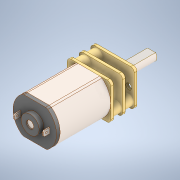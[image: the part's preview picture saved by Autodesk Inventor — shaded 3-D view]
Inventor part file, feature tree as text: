
AUTODESK INVENTOR PART (.ipt)
format: ipt  version: 2022 (Build 260153000, 153)  size: 256,000 bytes
history: mixed  units: mm
features: other x4, fillet x3, imported_body x1
ambient origin geometry x8: Origin, YZ Plane, XZ Plane, XY Plane, X Axis, Y Axis, Z Axis, Center Point
bodies: Solid1 (imported_parasolid), Solid2 (imported_parasolid), Solid3 (imported_parasolid), Solid4 (imported_parasolid), Solid5 (imported_parasolid), Solid6 (imported_parasolid), Solid7 (imported_parasolid)
feature tree (8):
  fillet  "Fillet1"  [1 undecoded]
  other  "Cut-Extrude3"
  other  "Boss-Extrude8[1]"
  other  "Boss-Extrude8[2]"
  fillet  "Fillet4"  [1 undecoded]
  fillet  "Fillet5"  [1 undecoded]
  other  "Cut-Extrude7"
  imported_body  NMx_Import_Brep_tag  [imported B-rep: ~119 faces, bbox_mm=[12.0, 10.0, 34.05]]
note: 3 required parameter values undecoded (feature->parameter linkage not recoverable at this tier; creation-order binding heuristic only, values carry confidence <= 0.55)
